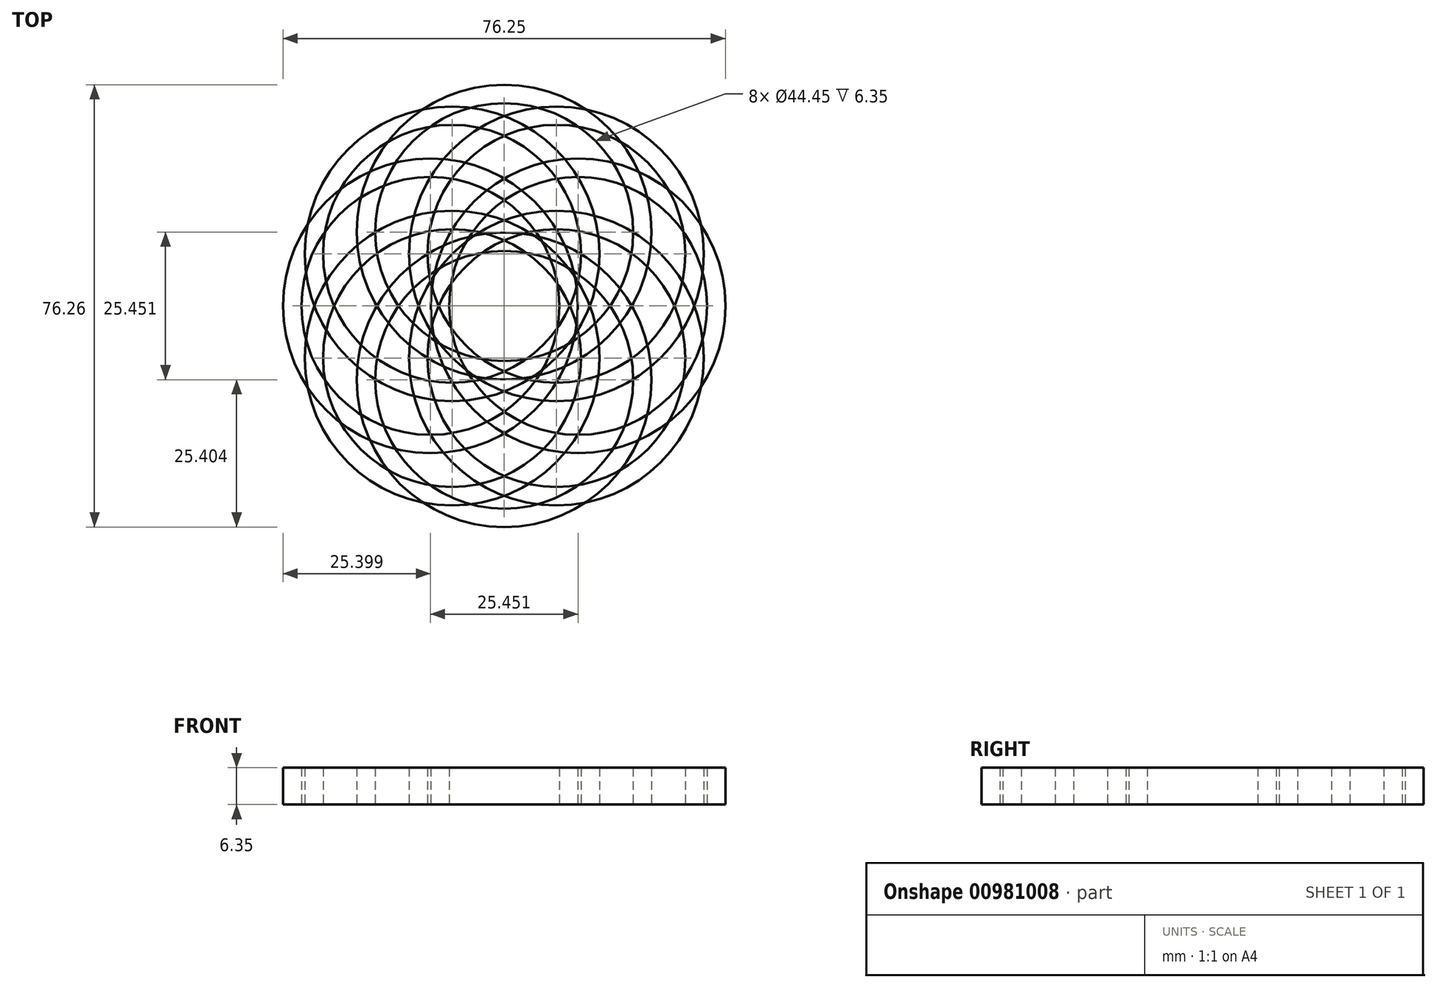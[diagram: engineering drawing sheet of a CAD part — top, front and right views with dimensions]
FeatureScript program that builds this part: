
annotation { "Feature Type Name" : "Feature", "Feature Type Description" : "" }
export const myFeature = defineFeature(function(context is Context, id is Id, definition is map)
    precondition{}
    {
        {
            var Q0;
            Q0=qCreatedBy(makeId("Top.planeOp"),FACE);
            var sketch = newSketch(context, id + "F0", { "sketchPlane" : qUnion([Q0])});
            skCircle(sketch, "E0", {"center": v(0, 0) * mm, "radius": 25.4 * mm});
            skSolve(sketch);
        }
        {
            var Q0;
            Q0 = qSketchRegion(id + "F0", true);
            extrude(context, id + "F1", {"entities" : qUnion([Q0]), "depth" : 6.35 * mm, "offsetDistance" : 25.4 * mm});
        }
        {
            var Q0;
            Q0=qCreatedBy(makeId("Top.planeOp"),FACE);
            var sketch = newSketch(context, id + "F2", { "sketchPlane" : qUnion([Q0])});
            skCircle(sketch, "E1", {"center": v(0, 0) * mm, "radius": 22.23 * mm});
            skSolve(sketch);
        }
        {
            var Q0;
            Q0 = qSketchRegion(id + "F2", true);
            extrude(context, id + "F3", {"entities" : qUnion([Q0]), "operationType" : NewBodyOperationType.REMOVE, "depth" : 25.4 * mm, "offsetDistance" : 25.4 * mm});
        }
        {
            var Q0;
            Q0=qCreatedBy(makeId("Front.planeOp"),FACE);
            var sketch = newSketch(context, id + "F4", { "sketchPlane" : qUnion([Q0])});
            skLineSegment(sketch, "E2", {"start": v(-12.73, 0) * mm, "end": v(-12.73, 6.82) * mm, "construction": true});
            skSolve(sketch);
        }
        {
            var Q0;
            Q0=makeQuery(id+"F1.opExtrude","SWEPT_BODY",BODY,{"disambiguationData":[OSD([sQuery(id+"F0.wireOp",EDGE,"E0")])]});
            var Q1;
            Q1=sQuery(id+"F4.wireOp",EDGE,"E2");
            circularPattern(context, id + "F5", {"entities" : qUnion([Q0]), "axis" : qUnion([Q1]), "angle" : 360 * degree, "instanceCount" : 8, "equalSpace" : true, "fullFeaturePattern" : false});
        }
    });
